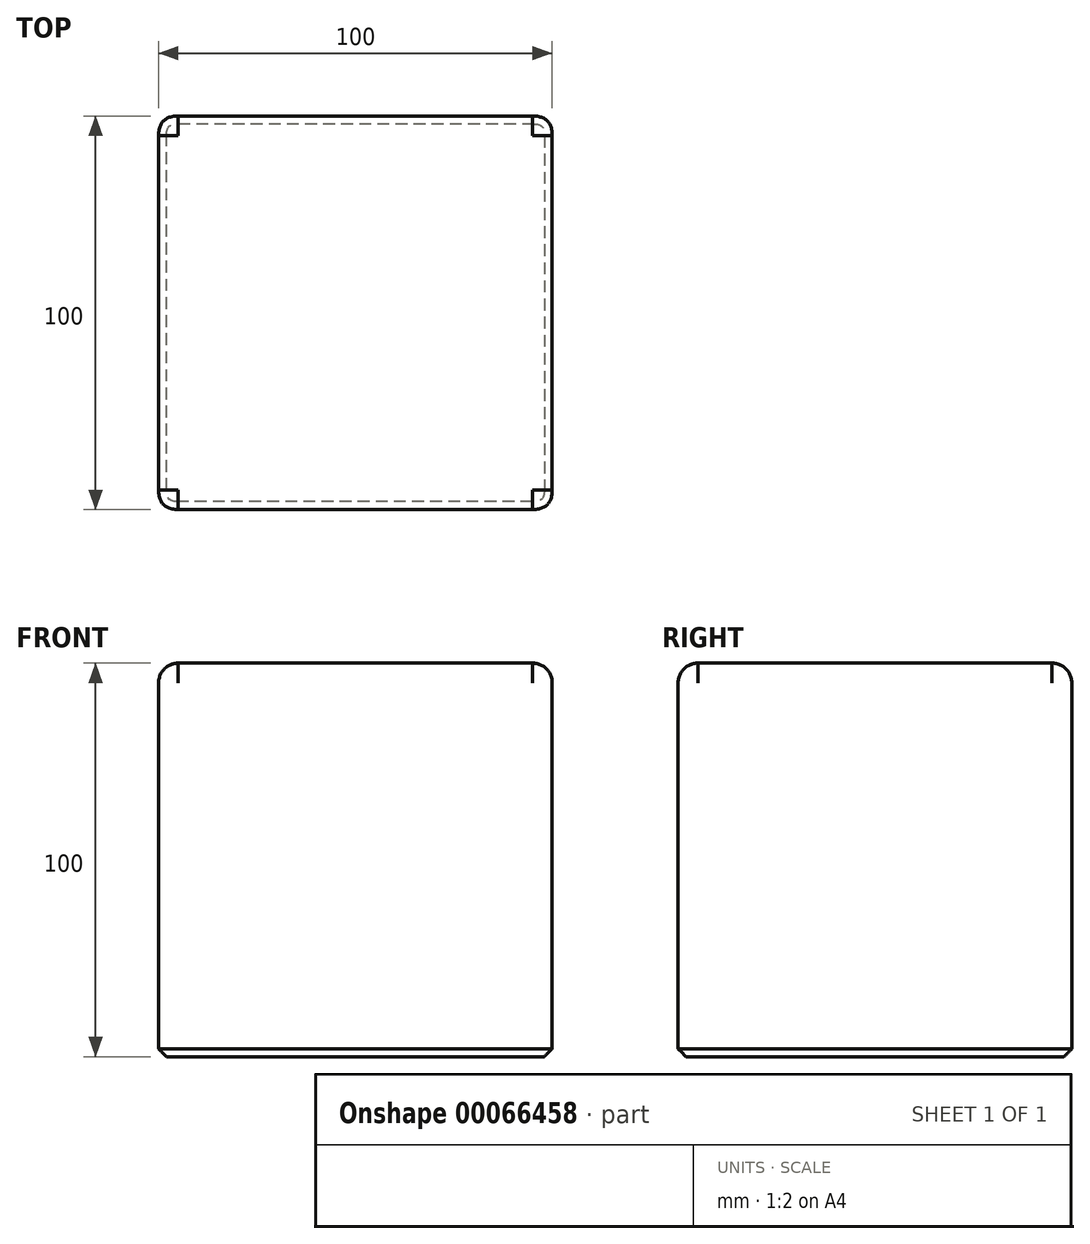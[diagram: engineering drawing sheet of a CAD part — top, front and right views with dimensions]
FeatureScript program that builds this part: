
annotation { "Feature Type Name" : "Feature", "Feature Type Description" : "" }
export const myFeature = defineFeature(function(context is Context, id is Id, definition is map)
    precondition{}
    {
        {
            var Q0;
            Q0=qCreatedBy(makeId("Right.planeOp"),FACE);
            var sketch = newSketch(context, id + "F0", { "sketchPlane" : qUnion([Q0])});
            skLineSegment(sketch, "E0.rect.bottom", {"start": v(50, 50) * mm, "end": v(-50, 50) * mm});
            skLineSegment(sketch, "E0.rect.top", {"start": v(50, -50) * mm, "end": v(-50, -50) * mm});
            skLineSegment(sketch, "E0.rect.left", {"start": v(50, 50) * mm, "end": v(50, -50) * mm});
            skLineSegment(sketch, "E0.rect.right", {"start": v(-50, 50) * mm, "end": v(-50, -50) * mm});
            skPoint(sketch, "E0.rect.middle", {"position": v(0, 0) * mm});
            skSolve(sketch);
        }
        {
            var Q0;
            Q0 = qSketchRegion(id + "F0", true);
            extrude(context, id + "F1", {"entities" : qUnion([Q0]), "endBound" : BoundingType.SYMMETRIC, "depth" : 100 * mm});
        }
        {
            var Q0;
            Q0=makeQuery(id+"F1.opExtrude","CAP_EDGE",EDGE,{"disambiguationData":[OSD([sQuery(id+"F0.wireOp",EDGE,"E0.rect.bottom")])],"isStart":false});
            var Q1;
            Q1=makeQuery(id+"F1.opExtrude","SWEPT_EDGE",EDGE,{"disambiguationData":[OSD([sQuery(id+"F0.wireOp",EDGE,"E0.rect.bottom"),sQuery(id+"F0.wireOp",EDGE,"E0.rect.right")])]});
            var Q2;
            Q2=makeQuery(id+"F1.opExtrude","CAP_EDGE",EDGE,{"disambiguationData":[OSD([sQuery(id+"F0.wireOp",EDGE,"E0.rect.bottom")])],"isStart":true});
            var Q3;
            Q3=makeQuery(id+"F1.opExtrude","SWEPT_EDGE",EDGE,{"disambiguationData":[OSD([sQuery(id+"F0.wireOp",EDGE,"E0.rect.bottom"),sQuery(id+"F0.wireOp",EDGE,"E0.rect.left")])]});
            fillet(context, id + "F2", {"entities" : qUnion([Q0, Q1, Q2, Q3]), "radius" : 5 * mm, "tangentPropagation" : true, "allowEdgeOverflow" : false});
        }
        {
            var Q0;
            Q0=makeQuery(id+"F1.opExtrude","CAP_EDGE",EDGE,{"disambiguationData":[OSD([sQuery(id+"F0.wireOp",EDGE,"E0.rect.right")])],"isStart":false});
            var Q1;
            Q1=makeQuery(id+"F1.opExtrude","CAP_EDGE",EDGE,{"disambiguationData":[OSD([sQuery(id+"F0.wireOp",EDGE,"E0.rect.left")])],"isStart":false});
            var Q2;
            Q2=makeQuery(id+"F1.opExtrude","CAP_EDGE",EDGE,{"disambiguationData":[OSD([sQuery(id+"F0.wireOp",EDGE,"E0.rect.left")])],"isStart":true});
            var Q3;
            Q3=makeQuery(id+"F1.opExtrude","CAP_EDGE",EDGE,{"disambiguationData":[OSD([sQuery(id+"F0.wireOp",EDGE,"E0.rect.right")])],"isStart":true});
            fillet(context, id + "F3", {"entities" : qUnion([Q0, Q1, Q2, Q3]), "radius" : 5 * mm, "tangentPropagation" : true, "rho" : 0.5, "crossSection" : FilletCrossSection.CONIC, "allowEdgeOverflow" : false});
        }
        {
            var Q0;
            Q0=makeQuery(id+"F1.opExtrude","SWEPT_EDGE",EDGE,{"disambiguationData":[OSD([sQuery(id+"F0.wireOp",EDGE,"E0.rect.top"),sQuery(id+"F0.wireOp",EDGE,"E0.rect.right")])]});
            var Q1;
            Q1=makeQuery(id+"F1.opExtrude","CAP_EDGE",EDGE,{"disambiguationData":[OSD([sQuery(id+"F0.wireOp",EDGE,"E0.rect.top")])],"isStart":true});
            var Q2;
            Q2=makeQuery(id+"F1.opExtrude","SWEPT_EDGE",EDGE,{"disambiguationData":[OSD([sQuery(id+"F0.wireOp",EDGE,"E0.rect.top"),sQuery(id+"F0.wireOp",EDGE,"E0.rect.left")])]});
            var Q3;
            Q3=makeQuery(id+"F1.opExtrude","CAP_EDGE",EDGE,{"disambiguationData":[OSD([sQuery(id+"F0.wireOp",EDGE,"E0.rect.top")])],"isStart":false});
            chamfer(context, id + "F4", {"entities" : qUnion([Q0, Q1, Q2, Q3]), "width" : 2 * mm, "tangentPropagation" : true});
        }
    });
